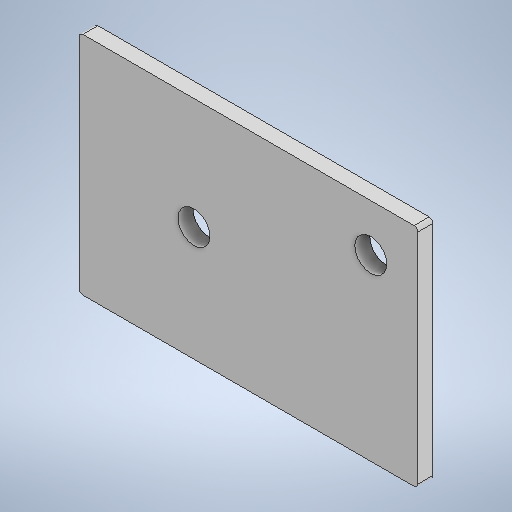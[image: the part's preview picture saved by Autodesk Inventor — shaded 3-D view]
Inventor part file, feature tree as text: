
AUTODESK INVENTOR PART (.ipt)
format: ipt  version: 2025 (Build 290162010, 162A)  size: 252,416 bytes
history: native  units: mm
features: sketch x2, other x2, sheet_metal_op x1, hole x1, fillet x1
ambient origin geometry x8: Origin, YZ Plane, XZ Plane, XY Plane, X Axis, Y Axis, Z Axis, Center Point
bodies: Solid1 (feature_tree)
feature tree (7):
  sheet_metal_op  "Face1"
  hole  "Hole1"  [1 undecoded]
  fillet  "Fillet1"  Radius=8.0mm
  sketch  "Sketch1"  dims[d0=180.0mm d1=120.0mm d2=8.0mm]
  other  "Plate1"
  sketch  "Sketch2"  dims[d3=17.0mm d4=6.0mm d5=4.0mm d6=2.0mm d7=90.0deg d8=8.0mm d9=20.594885mm d16=2.0mm d17=100.0mm d18=25.0mm d19=25.0mm d20=12.217305mm]
  other  "Definition1"
note: 1 required parameter value undecoded (feature->parameter linkage not recoverable at this tier; creation-order binding heuristic only, values carry confidence <= 0.55)
